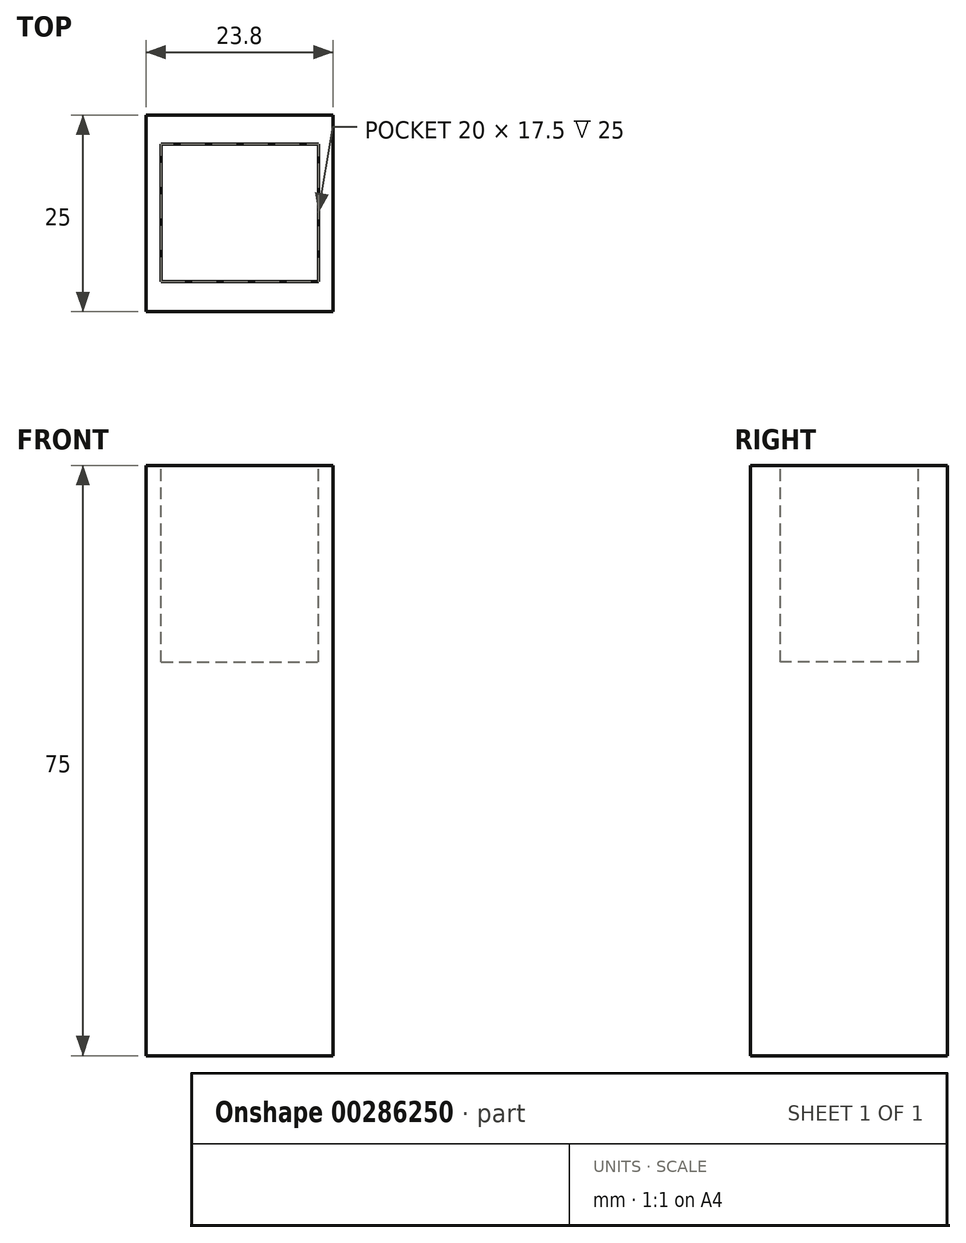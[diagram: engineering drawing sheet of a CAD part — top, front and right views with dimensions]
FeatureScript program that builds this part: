
annotation { "Feature Type Name" : "Feature", "Feature Type Description" : "" }
export const myFeature = defineFeature(function(context is Context, id is Id, definition is map)
    precondition{}
    {
        {
            var Q0;
            Q0=qCreatedBy(makeId("Right.planeOp"),FACE);
            var sketch = newSketch(context, id + "F0", { "sketchPlane" : qUnion([Q0])});
            skLineSegment(sketch, "E0.bottom", {"start": v(0, 0) * mm, "end": v(25, 0) * mm});
            skLineSegment(sketch, "E0.top", {"start": v(0, 75) * mm, "end": v(25, 75) * mm});
            skLineSegment(sketch, "E0.left", {"start": v(0, 0) * mm, "end": v(0, 75) * mm});
            skLineSegment(sketch, "E0.right", {"start": v(25, 0) * mm, "end": v(25, 75) * mm});
            skSolve(sketch);
        }
        {
            var Q0;
            Q0=makeQuery(id+"F0.imprint","IMPRINT",FACE,{"disambiguationData":[TD([[makeQuery(id+"F0.imprint","IMPRINT",EDGE,{"derivedFrom":sQuery(id+"F0.wireOp",EDGE,"E0.bottom")}),1.0]])]});
            extrude(context, id + "F1", {"entities" : qUnion([Q0]), "depth" : 23.8 * mm});
        }
        {
            var Q0;
            Q0=makeQuery(id+"F1.opExtrude","SWEPT_FACE",FACE,{"disambiguationData":[OSD([sQuery(id+"F0.wireOp",EDGE,"E0.top")])]});
            var sketch = newSketch(context, id + "F2", { "sketchPlane" : qUnion([Q0])});
            skLineSegment(sketch, "E1.bottom", {"start": v(1.93, 21.32) * mm, "end": v(21.93, 21.32) * mm});
            skLineSegment(sketch, "E1.top", {"start": v(1.93, 3.82) * mm, "end": v(21.93, 3.82) * mm});
            skLineSegment(sketch, "E1.left", {"start": v(1.93, 21.32) * mm, "end": v(1.93, 3.82) * mm});
            skLineSegment(sketch, "E1.right", {"start": v(21.93, 21.32) * mm, "end": v(21.93, 3.82) * mm});
            skSolve(sketch);
        }
        {
            var Q0;
            Q0=makeQuery(id+"F2.imprint","IMPRINT",FACE,{"disambiguationData":[TD([[makeQuery(id+"F2.imprint","IMPRINT",EDGE,{"derivedFrom":sQuery(id+"F2.wireOp",EDGE,"E1.bottom")}),-1.0]])]});
            extrude(context, id + "F3", {"entities" : qUnion([Q0]), "operationType" : NewBodyOperationType.REMOVE, "oppositeDirection" : true, "depth" : 25 * mm});
        }
    });
